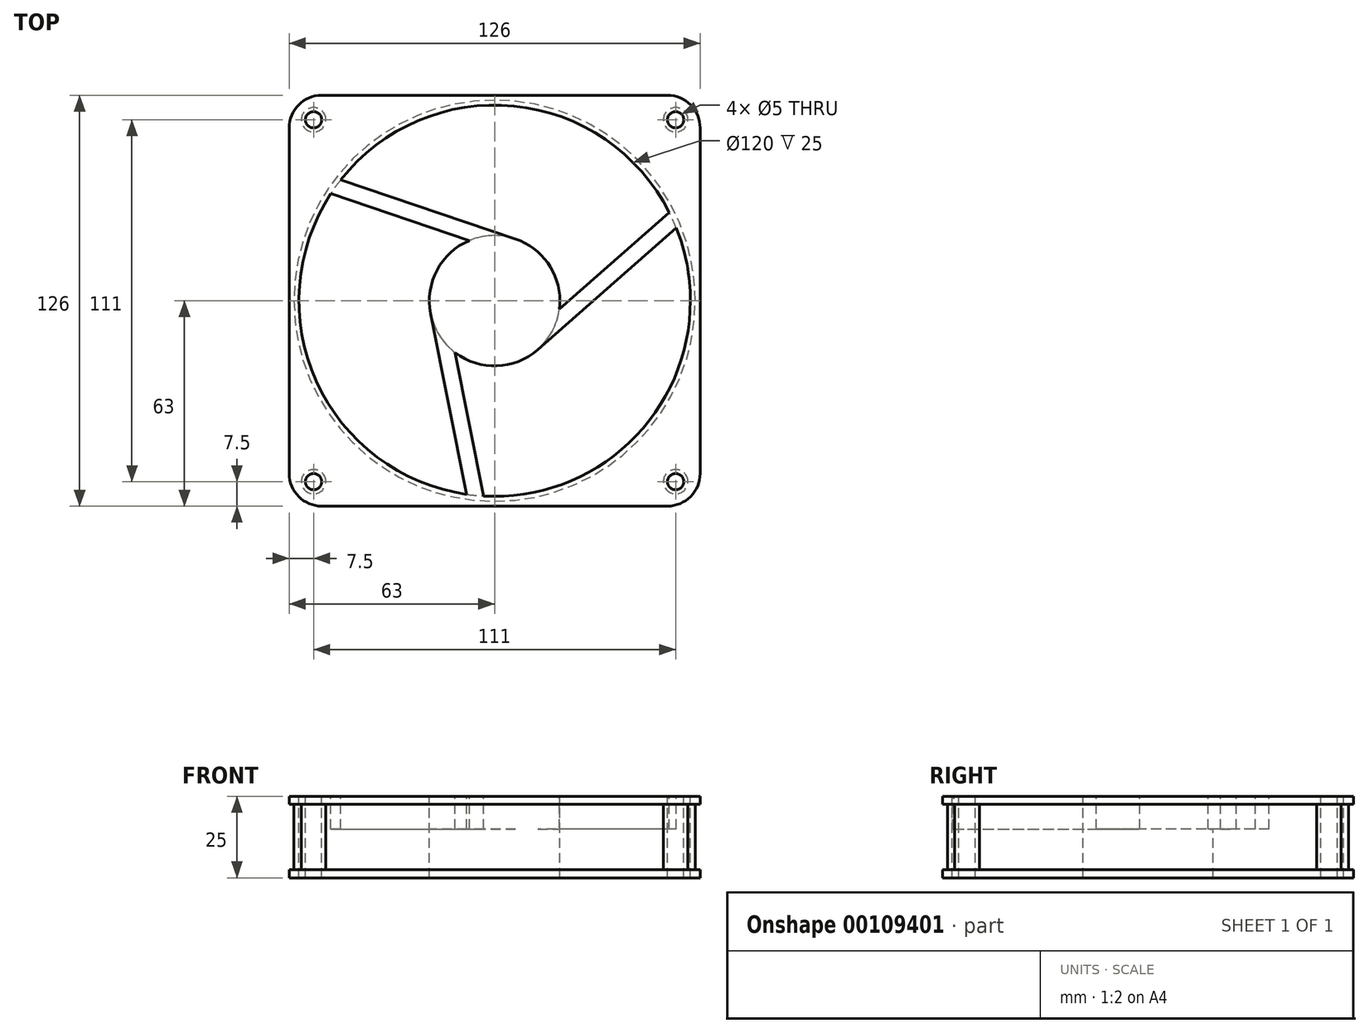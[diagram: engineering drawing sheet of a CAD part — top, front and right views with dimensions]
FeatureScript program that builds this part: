
annotation { "Feature Type Name" : "Feature", "Feature Type Description" : "" }
export const myFeature = defineFeature(function(context is Context, id is Id, definition is map)
    precondition{}
    {
        {
            var Q0;
            Q0=qCreatedBy(makeId("Top.planeOp"),FACE);
            var sketch = newSketch(context, id + "F0", { "sketchPlane" : qUnion([Q0])});
            skLineSegment(sketch, "E0.bottom", {"start": v(63, -63) * mm, "end": v(-63, -63) * mm});
            skLineSegment(sketch, "E0.top", {"start": v(63, 63) * mm, "end": v(-63, 63) * mm});
            skLineSegment(sketch, "E0.left", {"start": v(63, -63) * mm, "end": v(63, 63) * mm});
            skLineSegment(sketch, "E0.right", {"start": v(-63, -63) * mm, "end": v(-63, 63) * mm});
            skPoint(sketch, "E0.middle", {"position": v(0, 0) * mm});
            skSolve(sketch);
        }
        {
            var Q0;
            Q0 = qSketchRegion(id + "F0", true);
            extrude(context, id + "F1", {"entities" : qUnion([Q0]), "endBound" : BoundingType.SYMMETRIC, "depth" : 25 * mm});
        }
        {
            var Q0;
            Q0=makeQuery(id+"F1.opExtrude","CAP_FACE",FACE,{"disambiguationData":[OSD([sQuery(id+"F0.wireOp",EDGE,"E0.bottom"),sQuery(id+"F0.wireOp",EDGE,"E0.top"),sQuery(id+"F0.wireOp",EDGE,"E0.left"),sQuery(id+"F0.wireOp",EDGE,"E0.right")])],"isStart":false});
            var sketch = newSketch(context, id + "F6", { "sketchPlane" : qUnion([Q0])});
            skCircle(sketch, "E1", {"center": v(0, 0) * mm, "radius": 60 * mm});
            skCircle(sketch, "E2", {"center": v(0, 0) * mm, "radius": 20 * mm});
            skLineSegment(sketch, "E3.bottom", {"start": v(55.5, -55.5) * mm, "end": v(-55.5, -55.5) * mm, "construction": true});
            skLineSegment(sketch, "E3.top", {"start": v(55.5, 55.5) * mm, "end": v(-55.5, 55.5) * mm, "construction": true});
            skLineSegment(sketch, "E3.left", {"start": v(55.5, -55.5) * mm, "end": v(55.5, 55.5) * mm, "construction": true});
            skLineSegment(sketch, "E3.right", {"start": v(-55.5, -55.5) * mm, "end": v(-55.5, 55.5) * mm, "construction": true});
            skCircle(sketch, "E4", {"center": v(55.5, -55.5) * mm, "radius": 2.5 * mm});
            skCircle(sketch, "E5", {"center": v(-55.5, -55.5) * mm, "radius": 2.5 * mm});
            skCircle(sketch, "E6", {"center": v(-55.5, 55.5) * mm, "radius": 2.5 * mm});
            skCircle(sketch, "E7", {"center": v(55.5, 55.5) * mm, "radius": 2.5 * mm});
            skSolve(sketch);
        }
        {
            var Q0;
            Q0 = qSketchRegion(id + "F6", true);
            extrude(context, id + "F7", {"entities" : qUnion([Q0]), "operationType" : NewBodyOperationType.REMOVE, "endBound" : BoundingType.THROUGH_ALL, "oppositeDirection" : true, "depth" : 25.4 * mm});
        }
        {
            var Q0;
            Q0=makeQuery(id+"F7.boolean.opBoolean","SPLIT",FACE,{"disambiguationData":[TD([makeQuery(id+"F7.opExtrude","SWEPT_FACE",FACE,{"disambiguationData":[OSD([sQuery(id+"F6.wireOp",EDGE,"E2")])]})])],"derivedFrom":makeQuery(id+"F1.opExtrude","CAP_FACE",FACE,{"disambiguationData":[OSD([sQuery(id+"F0.wireOp",EDGE,"E0.bottom"),sQuery(id+"F0.wireOp",EDGE,"E0.top"),sQuery(id+"F0.wireOp",EDGE,"E0.left"),sQuery(id+"F0.wireOp",EDGE,"E0.right")])],"isStart":false})});
            var sketch = newSketch(context, id + "F2", { "sketchPlane" : qUnion([Q0])});
            skLineSegment(sketch, "E8", {"start": v(-47.16, 37.1) * mm, "end": v(6.42, 18.94) * mm});
            skLineSegment(sketch, "E9", {"start": v(-50.21, 32.85) * mm, "end": v(-7.72, 18.45) * mm});
            skArc(sketch, "E10.0", {"start": v(-47.16, 37.1) * mm, "mid": v(-48.73, 35) * mm, "end": v(-50.21, 32.85) * mm});
            skArc(sketch, "E11.0", {"start": v(6.42, 18.94) * mm, "mid": v(-0.7, 19.99) * mm, "end": v(-7.72, 18.45) * mm});
            skLineSegment(sketch, "E12.1.0", {"start": v(-3.34, -59.9) * mm, "end": v(-12.12, -15.9) * mm});
            skLineSegment(sketch, "E12.1.1", {"start": v(-8.54, -59.39) * mm, "end": v(-19.61, -3.91) * mm});
            skArc(sketch, "E12.1.2", {"start": v(-8.54, -59.39) * mm, "mid": v(-5.95, -59.7) * mm, "end": v(-3.34, -59.9) * mm});
            skArc(sketch, "E12.1.3", {"start": v(-19.61, -3.91) * mm, "mid": v(-16.96, -10.6) * mm, "end": v(-12.12, -15.9) * mm});
            skLineSegment(sketch, "E12.2.0", {"start": v(53.55, 27.06) * mm, "end": v(19.84, -2.54) * mm});
            skLineSegment(sketch, "E12.2.1", {"start": v(55.7, 22.3) * mm, "end": v(13.2, -15.03) * mm});
            skArc(sketch, "E12.2.2", {"start": v(55.7, 22.3) * mm, "mid": v(54.68, 24.7) * mm, "end": v(53.55, 27.06) * mm});
            skArc(sketch, "E12.2.3", {"start": v(13.2, -15.03) * mm, "mid": v(17.66, -9.4) * mm, "end": v(19.84, -2.54) * mm});
            skSolve(sketch);
        }
        {
            var Q0;
            Q0 = qSketchRegion(id + "F2", true);
            extrude(context, id + "F3", {"entities" : qUnion([Q0]), "operationType" : NewBodyOperationType.ADD, "oppositeDirection" : true, "depth" : 10 * mm});
        }
        {
            var Q0;
            Q0=qCreatedBy(makeId("Top.planeOp"),FACE);
            var sketch = newSketch(context, id + "F4", { "sketchPlane" : qUnion([Q0])});
            skCircle(sketch, "E13", {"center": v(0, 0) * mm, "radius": 61.5 * mm});
            skCircle(sketch, "E14", {"center": v(-55.5, 55.5) * mm, "radius": 3.75 * mm});
            skCircle(sketch, "E15", {"center": v(55.5, 55.5) * mm, "radius": 3.75 * mm});
            skCircle(sketch, "E16", {"center": v(55.5, -55.5) * mm, "radius": 3.75 * mm});
            skCircle(sketch, "E17", {"center": v(-55.5, -55.5) * mm, "radius": 3.75 * mm});
            skLineSegment(sketch, "E18.0", {"start": v(63, 63) * mm, "end": v(-63, 63) * mm});
            skLineSegment(sketch, "E19.1", {"start": v(-63, -63) * mm, "end": v(-63, 63) * mm});
            skLineSegment(sketch, "E20.2", {"start": v(63, -63) * mm, "end": v(-63, -63) * mm});
            skLineSegment(sketch, "E21.0", {"start": v(63, -63) * mm, "end": v(63, 63) * mm});
            skSolve(sketch);
        }
        {
            var Q0;
            Q0 = qSketchRegion(id + "F4", true);
            extrude(context, id + "F8", {"entities" : qUnion([Q0]), "operationType" : NewBodyOperationType.REMOVE, "endBound" : BoundingType.SYMMETRIC, "oppositeDirection" : true, "depth" : 20 * mm});
        }
        {
            var Q0;
            {var subQ0=sQuery(id+"F0.wireOp",EDGE,"E0.left");var subQ1=sQuery(id+"F0.wireOp",EDGE,"E0.top");Q0=makeQuery(id+"F8.boolean.opBoolean","SPLIT",EDGE,{"disambiguationData":[TD([makeQuery(id+"F1.opExtrude","CAP_FACE",FACE,{"disambiguationData":[OSD([sQuery(id+"F0.wireOp",EDGE,"E0.bottom"),subQ1,subQ0,sQuery(id+"F0.wireOp",EDGE,"E0.right")])],"isStart":true})])],"derivedFrom":makeQuery(id+"F1.opExtrude","SWEPT_EDGE",EDGE,{"disambiguationData":[OSD([subQ1,subQ0])]})});}
            var Q1;
            {var subQ0=sQuery(id+"F0.wireOp",EDGE,"E0.left");var subQ1=sQuery(id+"F0.wireOp",EDGE,"E0.top");Q1=makeQuery(id+"F8.boolean.opBoolean","SPLIT",EDGE,{"disambiguationData":[TD([makeQuery(id+"F1.opExtrude","CAP_FACE",FACE,{"disambiguationData":[OSD([sQuery(id+"F0.wireOp",EDGE,"E0.bottom"),subQ1,subQ0,sQuery(id+"F0.wireOp",EDGE,"E0.right")])],"isStart":false})])],"derivedFrom":makeQuery(id+"F1.opExtrude","SWEPT_EDGE",EDGE,{"disambiguationData":[OSD([subQ1,subQ0])]})});}
            var Q2;
            {var subQ0=sQuery(id+"F0.wireOp",EDGE,"E0.right");var subQ1=sQuery(id+"F0.wireOp",EDGE,"E0.top");Q2=makeQuery(id+"F8.boolean.opBoolean","SPLIT",EDGE,{"disambiguationData":[TD([makeQuery(id+"F1.opExtrude","CAP_FACE",FACE,{"disambiguationData":[OSD([sQuery(id+"F0.wireOp",EDGE,"E0.bottom"),subQ1,sQuery(id+"F0.wireOp",EDGE,"E0.left"),subQ0])],"isStart":false})])],"derivedFrom":makeQuery(id+"F1.opExtrude","SWEPT_EDGE",EDGE,{"disambiguationData":[OSD([subQ1,subQ0])]})});}
            var Q3;
            {var subQ0=sQuery(id+"F0.wireOp",EDGE,"E0.right");var subQ1=sQuery(id+"F0.wireOp",EDGE,"E0.top");Q3=makeQuery(id+"F8.boolean.opBoolean","SPLIT",EDGE,{"disambiguationData":[TD([makeQuery(id+"F1.opExtrude","CAP_FACE",FACE,{"disambiguationData":[OSD([sQuery(id+"F0.wireOp",EDGE,"E0.bottom"),subQ1,sQuery(id+"F0.wireOp",EDGE,"E0.left"),subQ0])],"isStart":true})])],"derivedFrom":makeQuery(id+"F1.opExtrude","SWEPT_EDGE",EDGE,{"disambiguationData":[OSD([subQ1,subQ0])]})});}
            var Q4;
            {var subQ0=sQuery(id+"F0.wireOp",EDGE,"E0.bottom");var subQ1=sQuery(id+"F0.wireOp",EDGE,"E0.right");Q4=makeQuery(id+"F8.boolean.opBoolean","SPLIT",EDGE,{"disambiguationData":[TD([makeQuery(id+"F1.opExtrude","CAP_FACE",FACE,{"disambiguationData":[OSD([subQ0,sQuery(id+"F0.wireOp",EDGE,"E0.top"),sQuery(id+"F0.wireOp",EDGE,"E0.left"),subQ1])],"isStart":true})])],"derivedFrom":makeQuery(id+"F1.opExtrude","SWEPT_EDGE",EDGE,{"disambiguationData":[OSD([subQ0,subQ1])]})});}
            var Q5;
            {var subQ0=sQuery(id+"F0.wireOp",EDGE,"E0.right");var subQ1=sQuery(id+"F0.wireOp",EDGE,"E0.bottom");Q5=makeQuery(id+"F8.boolean.opBoolean","SPLIT",EDGE,{"disambiguationData":[TD([makeQuery(id+"F1.opExtrude","CAP_FACE",FACE,{"disambiguationData":[OSD([subQ1,sQuery(id+"F0.wireOp",EDGE,"E0.top"),sQuery(id+"F0.wireOp",EDGE,"E0.left"),subQ0])],"isStart":false})])],"derivedFrom":makeQuery(id+"F1.opExtrude","SWEPT_EDGE",EDGE,{"disambiguationData":[OSD([subQ1,subQ0])]})});}
            var Q6;
            {var subQ0=sQuery(id+"F0.wireOp",EDGE,"E0.left");var subQ1=sQuery(id+"F0.wireOp",EDGE,"E0.bottom");Q6=makeQuery(id+"F8.boolean.opBoolean","SPLIT",EDGE,{"disambiguationData":[TD([makeQuery(id+"F1.opExtrude","CAP_FACE",FACE,{"disambiguationData":[OSD([subQ1,sQuery(id+"F0.wireOp",EDGE,"E0.top"),subQ0,sQuery(id+"F0.wireOp",EDGE,"E0.right")])],"isStart":false})])],"derivedFrom":makeQuery(id+"F1.opExtrude","SWEPT_EDGE",EDGE,{"disambiguationData":[OSD([subQ1,subQ0])]})});}
            var Q7;
            {var subQ0=sQuery(id+"F0.wireOp",EDGE,"E0.bottom");var subQ1=sQuery(id+"F0.wireOp",EDGE,"E0.left");Q7=makeQuery(id+"F8.boolean.opBoolean","SPLIT",EDGE,{"disambiguationData":[TD([makeQuery(id+"F1.opExtrude","CAP_FACE",FACE,{"disambiguationData":[OSD([subQ0,sQuery(id+"F0.wireOp",EDGE,"E0.top"),subQ1,sQuery(id+"F0.wireOp",EDGE,"E0.right")])],"isStart":true})])],"derivedFrom":makeQuery(id+"F1.opExtrude","SWEPT_EDGE",EDGE,{"disambiguationData":[OSD([subQ0,subQ1])]})});}
            fillet(context, id + "F5", {"entities" : qUnion([Q0, Q1, Q2, Q3, Q4, Q5, Q6, Q7]), "radius" : 10 * mm, "tangentPropagation" : true, "allowEdgeOverflow" : false});
        }
    });
